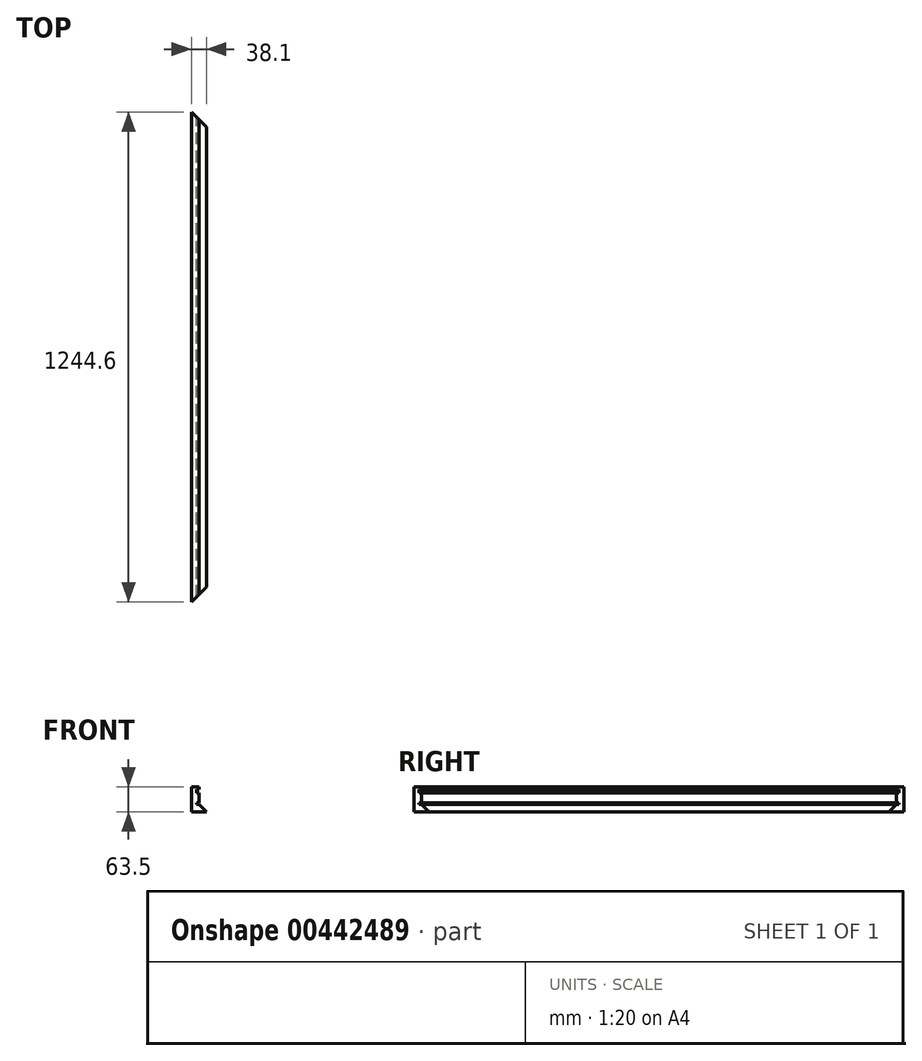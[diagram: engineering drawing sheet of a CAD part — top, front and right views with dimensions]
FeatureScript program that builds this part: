
annotation { "Feature Type Name" : "Feature", "Feature Type Description" : "" }
export const myFeature = defineFeature(function(context is Context, id is Id, definition is map)
    precondition{}
    {
        {
            var Q0;
            Q0=qCreatedBy(makeId("Front.planeOp"),FACE);
            var sketch = newSketch(context, id + "F0", { "sketchPlane" : qUnion([Q0])});
            skLineSegment(sketch, "E0", {"start": v(0, 62.16) * mm, "end": v(19.05, 62.16) * mm});
            skLineSegment(sketch, "E1", {"start": v(19.05, 62.16) * mm, "end": v(19.05, 55.8) * mm});
            skLineSegment(sketch, "E2", {"start": v(19.05, 55.8) * mm, "end": v(12.7, 55.8) * mm});
            skLineSegment(sketch, "E3", {"start": v(12.7, 55.8) * mm, "end": v(12.7, 47.17) * mm});
            skLineSegment(sketch, "E4", {"start": v(12.7, 47.17) * mm, "end": v(19.05, 47.17) * mm});
            skLineSegment(sketch, "E5", {"start": v(19.05, 47.17) * mm, "end": v(19.05, 21.77) * mm});
            skLineSegment(sketch, "E6", {"start": v(19.05, 21.77) * mm, "end": v(12.7, 21.77) * mm});
            skLineSegment(sketch, "E7", {"start": v(12.7, 21.77) * mm, "end": v(12.7, 17.7) * mm});
            skLineSegment(sketch, "E8", {"start": v(12.7, 17.7) * mm, "end": v(19.05, 17.7) * mm});
            skLineSegment(sketch, "E9", {"start": v(19.05, 17.7) * mm, "end": v(38.1, -1.34) * mm});
            skLineSegment(sketch, "E10", {"start": v(38.1, -1.34) * mm, "end": v(0, -1.34) * mm});
            skLineSegment(sketch, "E11", {"start": v(0, -1.34) * mm, "end": v(0, 62.16) * mm});
            skSolve(sketch);
        }
        {
            var Q0;
            Q0 = qSketchRegion(id + "F0", true);
            extrude(context, id + "F1", {"entities" : qUnion([Q0]), "depth" : 1244.6 * mm});
        }
        {
            var Q0;
            Q0=makeQuery(id+"F1.opExtrude","SWEPT_FACE",FACE,{"disambiguationData":[OSD([sQuery(id+"F0.wireOp",EDGE,"E0")])]});
            var sketch = newSketch(context, id + "F2", { "sketchPlane" : qUnion([Q0])});
            skLineSegment(sketch, "E12", {"start": v(0, 0) * mm, "end": v(38.1, 0) * mm});
            skLineSegment(sketch, "E13", {"start": v(38.1, 0) * mm, "end": v(38.1, -38.1) * mm});
            skLineSegment(sketch, "E14", {"start": v(38.1, -38.1) * mm, "end": v(0, 0) * mm});
            skLineSegment(sketch, "E15", {"start": v(0, -1244.6) * mm, "end": v(38.1, -1244.6) * mm});
            skLineSegment(sketch, "E16", {"start": v(38.1, -1244.6) * mm, "end": v(38.1, -1206.5) * mm});
            skLineSegment(sketch, "E17", {"start": v(38.1, -1206.5) * mm, "end": v(0, -1244.6) * mm});
            skSolve(sketch);
        }
        {
            var Q0;
            {var subQ1=sQuery(id+"F2.wireOp",EDGE,"E15");var subQ2=sQuery(id+"F0.wireOp",EDGE,"E0");var subQ4=makeQuery(id+"F1.opExtrude","SWEPT_EDGE",EDGE,{"disambiguationData":[OSD([subQ2,sQuery(id+"F0.wireOp",EDGE,"E1")])]});var subQ5=makeQuery(id+"F2.imprint","INTERSECT",VERTEX,{"derivedFrom":[subQ4,subQ1]});Q0=makeQuery(id+"F2.imprint","IMPRINT",FACE,{"disambiguationData":[TD([[makeQuery(id+"F2.imprint","IMPRINT",EDGE,{"disambiguationData":[TD([[subQ5,1.0]])],"derivedFrom":subQ1}),1.0]])]});}
            var Q1;
            {var subQ3=sQuery(id+"F2.wireOp",EDGE,"E16");Q1=makeQuery(id+"F2.imprint","IMPRINT",FACE,{"disambiguationData":[TD([[makeQuery(id+"F2.imprint","IMPRINT",EDGE,{"derivedFrom":subQ3}),1.0]])]});}
            var Q2;
            {var subQ1=sQuery(id+"F2.wireOp",EDGE,"E12");var subQ2=sQuery(id+"F0.wireOp",EDGE,"E0");var subQ4=makeQuery(id+"F1.opExtrude","SWEPT_EDGE",EDGE,{"disambiguationData":[OSD([subQ2,sQuery(id+"F0.wireOp",EDGE,"E1")])]});var subQ5=makeQuery(id+"F2.imprint","INTERSECT",VERTEX,{"derivedFrom":[subQ4,subQ1]});Q2=makeQuery(id+"F2.imprint","IMPRINT",FACE,{"disambiguationData":[TD([[makeQuery(id+"F2.imprint","IMPRINT",EDGE,{"disambiguationData":[TD([[subQ5,1.0]])],"derivedFrom":subQ1}),-1.0]])]});}
            var Q3;
            {var subQ3=sQuery(id+"F2.wireOp",EDGE,"E13");Q3=makeQuery(id+"F2.imprint","IMPRINT",FACE,{"disambiguationData":[TD([[makeQuery(id+"F2.imprint","IMPRINT",EDGE,{"derivedFrom":subQ3}),-1.0]])]});}
            extrude(context, id + "F3", {"entities" : qUnion([Q0, Q1, Q2, Q3]), "operationType" : NewBodyOperationType.REMOVE, "oppositeDirection" : true, "depth" : 63.5 * mm});
        }
    });
